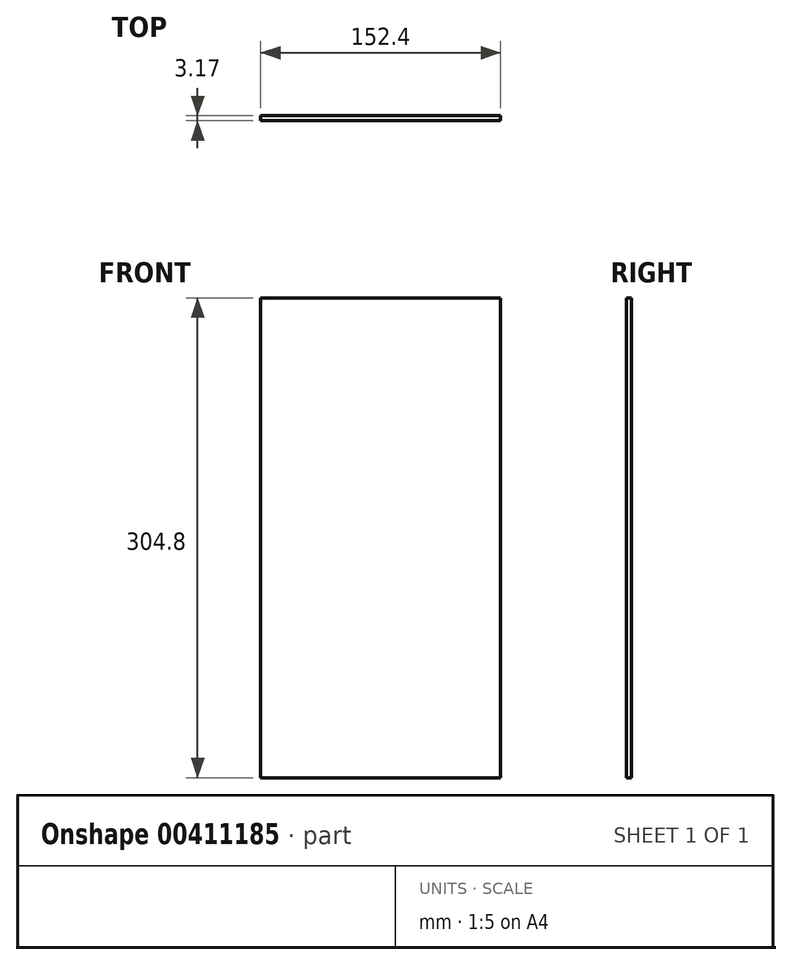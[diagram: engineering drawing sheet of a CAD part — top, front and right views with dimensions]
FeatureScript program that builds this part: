
annotation { "Feature Type Name" : "Feature", "Feature Type Description" : "" }
export const myFeature = defineFeature(function(context is Context, id is Id, definition is map)
    precondition{}
    {
        {
            var Q0;
            Q0=qCreatedBy(makeId("Front.planeOp"),FACE);
            var sketch = newSketch(context, id + "F0", { "sketchPlane" : qUnion([Q0])});
            skLineSegment(sketch, "E0.bottom", {"start": v(-76.2, 152.4) * mm, "end": v(76.2, 152.4) * mm});
            skLineSegment(sketch, "E0.top", {"start": v(-76.2, -152.4) * mm, "end": v(76.2, -152.4) * mm});
            skLineSegment(sketch, "E0.left", {"start": v(-76.2, 152.4) * mm, "end": v(-76.2, -152.4) * mm});
            skLineSegment(sketch, "E0.right", {"start": v(76.2, 152.4) * mm, "end": v(76.2, -152.4) * mm});
            skPoint(sketch, "E0.middle", {"position": v(0, 0) * mm});
            skSolve(sketch);
        }
        {
            var Q0;
            Q0 = qSketchRegion(id + "F0", true);
            extrude(context, id + "F1", {"entities" : qUnion([Q0]), "depth" : 3.17 * mm});
        }
    });
